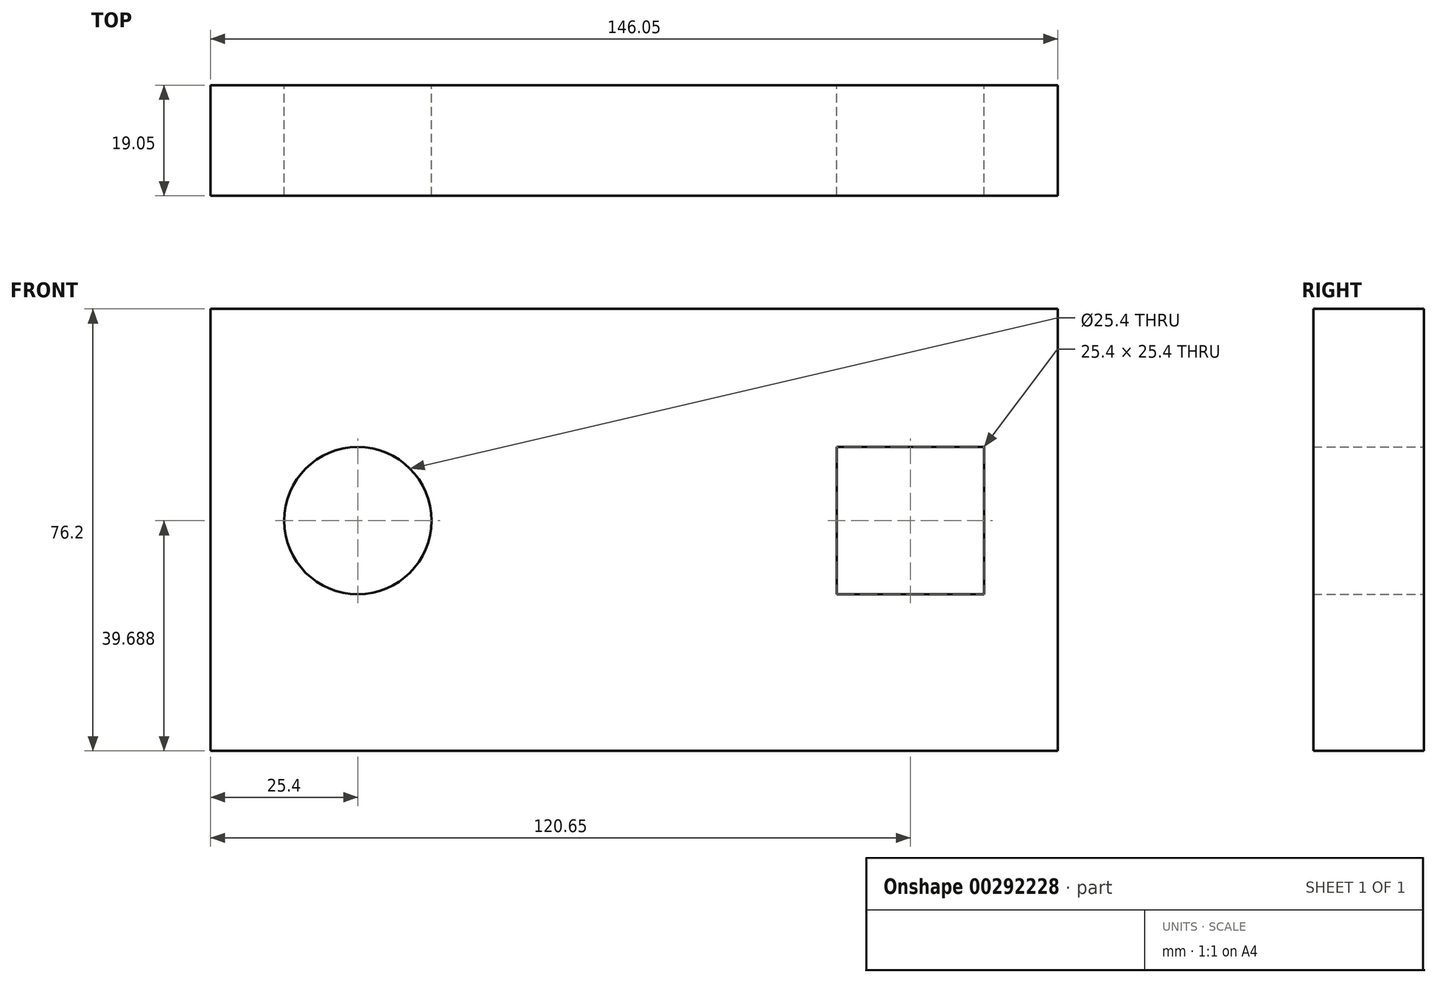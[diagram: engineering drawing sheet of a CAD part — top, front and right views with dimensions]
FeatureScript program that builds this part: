
annotation { "Feature Type Name" : "Feature", "Feature Type Description" : "" }
export const myFeature = defineFeature(function(context is Context, id is Id, definition is map)
    precondition{}
    {
        {
            var Q0;
            Q0=qCreatedBy(makeId("Front.planeOp"),FACE);
            var sketch = newSketch(context, id + "F0", { "sketchPlane" : qUnion([Q0])});
            skLineSegment(sketch, "E0.bottom", {"start": v(0, 0) * mm, "end": v(-146.05, 0) * mm});
            skLineSegment(sketch, "E0.top", {"start": v(0, 76.2) * mm, "end": v(-146.05, 76.2) * mm});
            skLineSegment(sketch, "E0.left", {"start": v(0, 0) * mm, "end": v(0, 76.2) * mm});
            skLineSegment(sketch, "E0.right", {"start": v(-146.05, 0) * mm, "end": v(-146.05, 76.2) * mm});
            skCircle(sketch, "E1", {"center": v(-120.65, 39.69) * mm, "radius": 12.7 * mm});
            skLineSegment(sketch, "E2.bottom", {"start": v(-38.1, 52.39) * mm, "end": v(-12.7, 52.39) * mm});
            skLineSegment(sketch, "E2.top", {"start": v(-38.1, 26.99) * mm, "end": v(-12.7, 26.99) * mm});
            skLineSegment(sketch, "E2.left", {"start": v(-38.1, 52.39) * mm, "end": v(-38.1, 26.99) * mm});
            skLineSegment(sketch, "E2.right", {"start": v(-12.7, 52.39) * mm, "end": v(-12.7, 26.99) * mm});
            skPoint(sketch, "E2.middle", {"position": v(-25.4, 39.69) * mm});
            skSolve(sketch);
        }
        {
            var Q0;
            Q0 = qSketchRegion(id + "F0", true);
            extrude(context, id + "F1", {"entities" : qUnion([Q0]), "depth" : 19.05 * mm});
        }
    });
